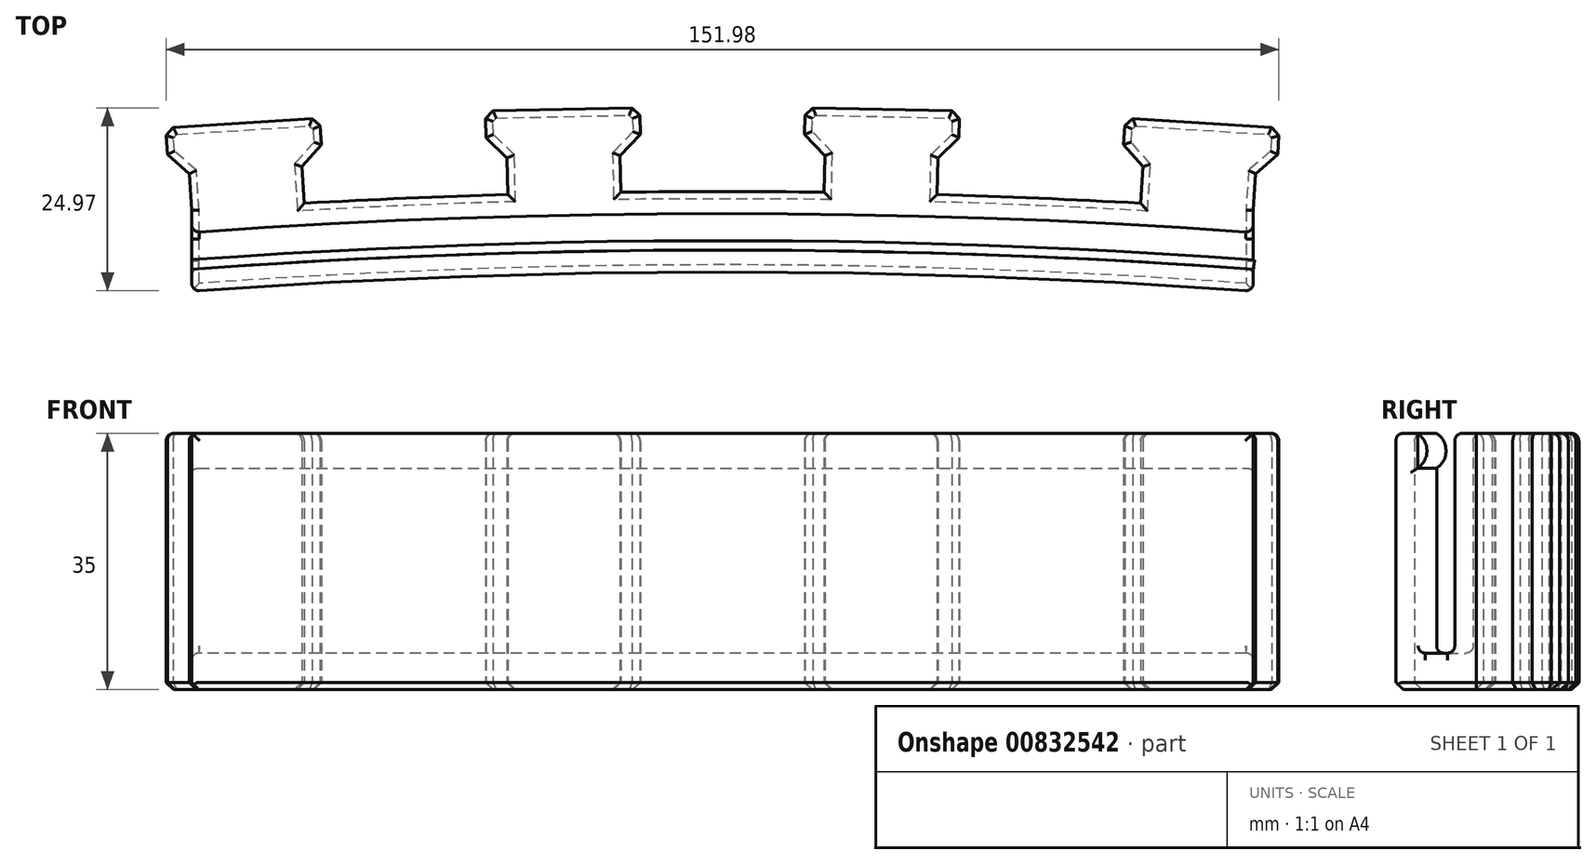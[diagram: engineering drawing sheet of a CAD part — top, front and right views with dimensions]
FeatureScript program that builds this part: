
annotation { "Feature Type Name" : "Feature", "Feature Type Description" : "" }
export const myFeature = defineFeature(function(context is Context, id is Id, definition is map)
    precondition{}
    {
        {
            var Q0;
            Q0=qCreatedBy(makeId("Top.planeOp"),FACE);
            var sketch = newSketch(context, id + "F0", { "sketchPlane" : qUnion([Q0])});
            skArc(sketch, "E0", {"start": v(72.5, 0) * mm, "mid": v(0, 2.6) * mm, "end": v(-72.5, 0) * mm});
            skPoint(sketch, "E1", {"position": v(0, 2.6) * mm});
            skArc(sketch, "E2.0", {"start": v(72.5, 3) * mm, "mid": v(0, 5.6) * mm, "end": v(-72.5, 3) * mm});
            skArc(sketch, "E3.0", {"start": v(72.5, -5.01) * mm, "mid": v(0, -2.4) * mm, "end": v(-72.5, -5.01) * mm});
            skArc(sketch, "E4.0", {"start": v(72.5, -8.02) * mm, "mid": v(0, -5.4) * mm, "end": v(-72.5, -8.02) * mm});
            skLineSegment(sketch, "E5", {"start": v(-72.5, -5.01) * mm, "end": v(-72.5, -8.02) * mm});
            skLineSegment(sketch, "E6", {"start": v(-72.5, 3) * mm, "end": v(-72.5, 0) * mm});
            skLineSegment(sketch, "E7", {"start": v(72.5, 3) * mm, "end": v(72.5, 0) * mm});
            skLineSegment(sketch, "E8", {"start": v(72.5, -5.01) * mm, "end": v(72.5, -8.02) * mm});
            skLineSegment(sketch, "E9", {"start": v(-72.5, 3) * mm, "end": v(-72.5, -8.02) * mm});
            skLineSegment(sketch, "E10", {"start": v(72.5, 3) * mm, "end": v(72.5, -8.02) * mm});
            skPoint(sketch, "E11", {"position": v(-21.6, 5.36) * mm});
            skPoint(sketch, "E12", {"position": v(21.6, 5.36) * mm});
            skSolve(sketch);
        }
        {
            var Q0;
            {var subQ0=sQuery(id+"F0.wireOp",EDGE,"E0");Q0=makeQuery(id+"F0.imprint","IMPRINT",FACE,{"disambiguationData":[TD([[makeQuery(id+"F0.imprint","IMPRINT",EDGE,{"derivedFrom":subQ0}),1.0]])]});}
            var Q1;
            {var subQ0=sQuery(id+"F0.wireOp",EDGE,"E0");Q1=makeQuery(id+"F0.imprint","IMPRINT",FACE,{"disambiguationData":[TD([[makeQuery(id+"F0.imprint","IMPRINT",EDGE,{"derivedFrom":subQ0}),-1.0]])]});}
            var Q2;
            {var subQ0=sQuery(id+"F0.wireOp",EDGE,"E3.0");Q2=makeQuery(id+"F0.imprint","IMPRINT",FACE,{"disambiguationData":[TD([[makeQuery(id+"F0.imprint","IMPRINT",EDGE,{"derivedFrom":subQ0}),1.0]])]});}
            extrude(context, id + "F1", {"entities" : qUnion([Q0, Q1, Q2]), "depth" : 5 * mm, "offsetDistance" : 25 * mm});
        }
        {
            var Q0;
            {var subQ0=sQuery(id+"F0.wireOp",EDGE,"E0");Q0=makeQuery(id+"F0.imprint","IMPRINT",FACE,{"disambiguationData":[TD([[makeQuery(id+"F0.imprint","IMPRINT",EDGE,{"derivedFrom":subQ0}),-1.0]])]});}
            extrude(context, id + "F2", {"entities" : qUnion([Q0]), "operationType" : NewBodyOperationType.ADD, "depth" : 35 * mm, "offsetDistance" : 25 * mm});
        }
        {
            var Q0;
            {var subQ0=sQuery(id+"F0.wireOp",EDGE,"E3.0");Q0=makeQuery(id+"F0.imprint","IMPRINT",FACE,{"disambiguationData":[TD([[makeQuery(id+"F0.imprint","IMPRINT",EDGE,{"derivedFrom":subQ0}),1.0]])]});}
            var Q1;
            Q1=makeQuery(id+"F2.opExtrude","CAP_FACE",FACE,{"disambiguationData":[OSD([sQuery(id+"F0.wireOp",EDGE,"E0"),sQuery(id+"F0.wireOp",EDGE,"E2.0"),sQuery(id+"F0.wireOp",EDGE,"E9"),sQuery(id+"F0.wireOp",EDGE,"E10")])],"isStart":false});
            extrude(context, id + "F3", {"entities" : qUnion([Q0]), "operationType" : NewBodyOperationType.ADD, "endBound" : BoundingType.UP_TO_SURFACE, "depth" : 35 * mm, "endBoundEntityFace" : qUnion([Q1]), "offsetDistance" : 25 * mm});
        }
        {
            var Q0;
            {var subQ0=sQuery(id+"F0.wireOp",EDGE,"E9");Q0=makeQuery(id+"F3.boolean.opBoolean","MERGE",FACE,{"derivedFrom":[makeQuery(id+"F2.boolean.opBoolean","MERGE",FACE,{"derivedFrom":[makeQuery(id+"F1.opExtrude","SWEPT_FACE",FACE,{"disambiguationData":[OSD([subQ0])]}),makeQuery(id+"F2.opExtrude","SWEPT_FACE",FACE,{"disambiguationData":[OSD([subQ0])]})]}),makeQuery(id+"F3.opExtrude","SWEPT_FACE",FACE,{"disambiguationData":[OSD([subQ0])]})]});}
            var sketch = newSketch(context, id + "F4", { "sketchPlane" : qUnion([Q0])});
            skArc(sketch, "E13", {"start": v(5.01, 35) * mm, "mid": v(3.72, 32.62) * mm, "end": v(5.01, 30.24) * mm});
            skSolve(sketch);
        }
        {
            var Q0;
            {var subQ0=sQuery(id+"F4.wireOp",EDGE,"E13");Q0=makeQuery(id+"F4.imprint","IMPRINT",FACE,{"disambiguationData":[TD([[makeQuery(id+"F4.imprint","IMPRINT",EDGE,{"derivedFrom":subQ0}),1.0]])]});}
            var Q1;
            Q1=makeQuery(id+"F3.opExtrude","CAP_EDGE",EDGE,{"disambiguationData":[OSD([sQuery(id+"F0.wireOp",EDGE,"E3.0")])],"isStart":false});
            sweep(context, id + "F5", {"operationType" : NewBodyOperationType.ADD, "profiles" : qUnion([Q0]), "path" : qUnion([Q1])});
        }
        {
            var Q0;
            Q0=qCreatedBy(makeId("Top.planeOp"),FACE);
            var sketch = newSketch(context, id + "F6", { "sketchPlane" : qUnion([Q0])});
            skLineSegment(sketch, "E14", {"start": v(57.11, 3.99) * mm, "end": v(72.5, 3) * mm});
            skLineSegment(sketch, "E15", {"start": v(57.11, 3.99) * mm, "end": v(57.43, 8.98) * mm});
            skLineSegment(sketch, "E16", {"start": v(72.5, 3) * mm, "end": v(72.82, 8) * mm});
            skLineSegment(sketch, "E17", {"start": v(72.82, 8) * mm, "end": v(75.82, 10.64) * mm});
            skLineSegment(sketch, "E18", {"start": v(75.02, 14.36) * mm, "end": v(56.06, 15.57) * mm});
            skLineSegment(sketch, "E19", {"start": v(54.79, 11.98) * mm, "end": v(57.43, 8.98) * mm});
            skLineSegment(sketch, "E20", {"start": v(54.79, 11.98) * mm, "end": v(54.95, 14.6) * mm});
            skLineSegment(sketch, "E21", {"start": v(54.95, 14.6) * mm, "end": v(56.06, 15.57) * mm});
            skLineSegment(sketch, "E22", {"start": v(75.02, 14.36) * mm, "end": v(76, 13.25) * mm});
            skLineSegment(sketch, "E23", {"start": v(76, 13.25) * mm, "end": v(75.82, 10.64) * mm});
            skPoint(sketch, "E24", {"position": v(65.54, 14.96) * mm});
            skPoint(sketch, "E25", {"position": v(64.8, 3.5) * mm});
            skLineSegment(sketch, "E26", {"start": v(66.13, 24.3) * mm, "end": v(62.81, -27.83) * mm, "construction": true});
            skLineSegment(sketch, "E27", {"start": v(53.84, 9.2) * mm, "end": v(75.99, 7.8) * mm, "construction": true});
            skLineSegment(sketch, "E28", {"start": v(54.06, 12.03) * mm, "end": v(76.55, 10.6) * mm, "construction": true});
            skLineSegment(sketch, "E29", {"start": v(57.43, 14.44) * mm, "end": v(80.73, 12.95) * mm, "construction": true});
            skPoint(sketch, "E30", {"position": v(65.3, 11.31) * mm});
            skSolve(sketch);
        }
        {
            var Q0;
            Q0=qCreatedBy(makeId("Top.planeOp"),FACE);
            var sketch = newSketch(context, id + "F7", { "sketchPlane" : qUnion([Q0])});
            skLineSegment(sketch, "E31", {"start": v(-72.5, 3) * mm, "end": v(-57.11, 3.99) * mm});
            skLineSegment(sketch, "E32", {"start": v(-72.5, 3) * mm, "end": v(-72.82, 8) * mm});
            skLineSegment(sketch, "E33", {"start": v(-57.11, 3.99) * mm, "end": v(-57.43, 8.98) * mm});
            skLineSegment(sketch, "E34", {"start": v(-57.43, 8.98) * mm, "end": v(-54.79, 11.98) * mm});
            skLineSegment(sketch, "E35", {"start": v(-56.06, 15.57) * mm, "end": v(-75.02, 14.36) * mm});
            skLineSegment(sketch, "E36", {"start": v(-75.82, 10.64) * mm, "end": v(-72.82, 8) * mm});
            skLineSegment(sketch, "E37", {"start": v(-75.82, 10.64) * mm, "end": v(-76, 13.25) * mm});
            skLineSegment(sketch, "E38", {"start": v(-76, 13.25) * mm, "end": v(-75.02, 14.36) * mm});
            skLineSegment(sketch, "E39", {"start": v(-56.06, 15.57) * mm, "end": v(-54.95, 14.6) * mm});
            skLineSegment(sketch, "E40", {"start": v(-54.95, 14.6) * mm, "end": v(-54.79, 11.98) * mm});
            skPoint(sketch, "E41", {"position": v(-65.54, 14.96) * mm});
            skPoint(sketch, "E42", {"position": v(-64.8, 3.5) * mm});
            skLineSegment(sketch, "E43", {"start": v(-66.36, 27.87) * mm, "end": v(-63.01, -24.64) * mm, "construction": true});
            skLineSegment(sketch, "E44", {"start": v(-77.11, 7.72) * mm, "end": v(-54.85, 9.14) * mm, "construction": true});
            skLineSegment(sketch, "E45", {"start": v(-77.54, 10.53) * mm, "end": v(-55.06, 11.97) * mm, "construction": true});
            skLineSegment(sketch, "E46", {"start": v(-74.75, 13.33) * mm, "end": v(-51.32, 14.83) * mm, "construction": true});
            skPoint(sketch, "E47", {"position": v(-65.3, 11.31) * mm});
            skSolve(sketch);
        }
        {
            var Q0;
            Q0=qCreatedBy(makeId("Top.planeOp"),FACE);
            var sketch = newSketch(context, id + "F8", { "sketchPlane" : qUnion([Q0])});
            skLineSegment(sketch, "E48", {"start": v(-29.3, 5.17) * mm, "end": v(-13.9, 5.5) * mm});
            skLineSegment(sketch, "E49", {"start": v(-29.3, 5.17) * mm, "end": v(-29.41, 10.17) * mm});
            skLineSegment(sketch, "E50", {"start": v(-13.9, 5.5) * mm, "end": v(-14, 10.5) * mm});
            skLineSegment(sketch, "E51", {"start": v(-14, 10.5) * mm, "end": v(-11.23, 13.39) * mm});
            skLineSegment(sketch, "E52", {"start": v(-12.35, 17.02) * mm, "end": v(-31.34, 16.62) * mm});
            skLineSegment(sketch, "E53", {"start": v(-32.3, 12.94) * mm, "end": v(-29.41, 10.17) * mm});
            skLineSegment(sketch, "E54", {"start": v(-32.3, 12.94) * mm, "end": v(-32.36, 15.55) * mm});
            skLineSegment(sketch, "E55", {"start": v(-32.36, 15.55) * mm, "end": v(-31.34, 16.62) * mm});
            skLineSegment(sketch, "E56", {"start": v(-12.35, 17.02) * mm, "end": v(-11.28, 16) * mm});
            skLineSegment(sketch, "E57", {"start": v(-11.28, 16) * mm, "end": v(-11.23, 13.39) * mm});
            skPoint(sketch, "E58", {"position": v(-21.84, 16.82) * mm});
            skPoint(sketch, "E59", {"position": v(-21.6, 5.33) * mm});
            skLineSegment(sketch, "E60", {"start": v(-22.4, 42.7) * mm, "end": v(-21.1, -18.04) * mm, "construction": true});
            skLineSegment(sketch, "E61", {"start": v(-33.71, 10.08) * mm, "end": v(-11.41, 10.55) * mm, "construction": true});
            skLineSegment(sketch, "E62", {"start": v(-34.02, 12.9) * mm, "end": v(-11.5, 13.38) * mm, "construction": true});
            skLineSegment(sketch, "E63", {"start": v(-31.12, 15.58) * mm, "end": v(-7.65, 16.08) * mm, "construction": true});
            skPoint(sketch, "E64", {"position": v(-21.77, 13.16) * mm});
            skSolve(sketch);
        }
        {
            var Q0;
            Q0=qCreatedBy(makeId("Top.planeOp"),FACE);
            var sketch = newSketch(context, id + "F9", { "sketchPlane" : qUnion([Q0])});
            skLineSegment(sketch, "E65", {"start": v(13.9, 5.5) * mm, "end": v(29.3, 5.17) * mm});
            skLineSegment(sketch, "E66", {"start": v(13.9, 5.5) * mm, "end": v(14, 10.5) * mm});
            skLineSegment(sketch, "E67", {"start": v(29.3, 5.17) * mm, "end": v(29.41, 10.17) * mm});
            skLineSegment(sketch, "E68", {"start": v(29.41, 10.17) * mm, "end": v(32.3, 12.94) * mm});
            skLineSegment(sketch, "E69", {"start": v(31.34, 16.62) * mm, "end": v(12.35, 17.02) * mm});
            skLineSegment(sketch, "E70", {"start": v(11.23, 13.39) * mm, "end": v(14, 10.5) * mm});
            skLineSegment(sketch, "E71", {"start": v(11.23, 13.39) * mm, "end": v(11.28, 16) * mm});
            skLineSegment(sketch, "E72", {"start": v(11.28, 16) * mm, "end": v(12.35, 17.02) * mm});
            skLineSegment(sketch, "E73", {"start": v(31.34, 16.62) * mm, "end": v(32.36, 15.55) * mm});
            skLineSegment(sketch, "E74", {"start": v(32.36, 15.55) * mm, "end": v(32.3, 12.94) * mm});
            skPoint(sketch, "E75", {"position": v(21.84, 16.82) * mm});
            skPoint(sketch, "E76", {"position": v(21.6, 5.33) * mm});
            skLineSegment(sketch, "E77", {"start": v(22.43, 44.36) * mm, "end": v(20.9, -27.94) * mm, "construction": true});
            skLineSegment(sketch, "E78", {"start": v(9.7, 10.59) * mm, "end": v(32, 10.11) * mm, "construction": true});
            skLineSegment(sketch, "E79", {"start": v(9.51, 13.42) * mm, "end": v(32.03, 12.94) * mm, "construction": true});
            skLineSegment(sketch, "E80", {"start": v(12.52, 15.98) * mm, "end": v(36, 15.48) * mm, "construction": true});
            skPoint(sketch, "E81", {"position": v(21.77, 13.16) * mm});
            skSolve(sketch);
        }
        {
            var Q0;
            Q0=makeQuery(id+"F7.imprint","IMPRINT",FACE,{"disambiguationData":[TD([[makeQuery(id+"F7.imprint","IMPRINT",EDGE,{"derivedFrom":sQuery(id+"F7.wireOp",EDGE,"E31")}),1.0]])]});
            var Q1;
            Q1=makeQuery(id+"F6.imprint","IMPRINT",FACE,{"disambiguationData":[TD([[makeQuery(id+"F6.imprint","IMPRINT",EDGE,{"derivedFrom":sQuery(id+"F6.wireOp",EDGE,"E14")}),1.0]])]});
            var Q2;
            Q2=makeQuery(id+"F9.imprint","IMPRINT",FACE,{"disambiguationData":[TD([[makeQuery(id+"F9.imprint","IMPRINT",EDGE,{"derivedFrom":sQuery(id+"F9.wireOp",EDGE,"E65")}),1.0]])]});
            var Q3;
            Q3=makeQuery(id+"F8.imprint","IMPRINT",FACE,{"disambiguationData":[TD([[makeQuery(id+"F8.imprint","IMPRINT",EDGE,{"derivedFrom":sQuery(id+"F8.wireOp",EDGE,"E48")}),1.0]])]});
            var Q4;
            Q4=makeQuery(id+"F2.opExtrude","CAP_FACE",FACE,{"disambiguationData":[OSD([sQuery(id+"F0.wireOp",EDGE,"E0"),sQuery(id+"F0.wireOp",EDGE,"E2.0"),sQuery(id+"F0.wireOp",EDGE,"E9"),sQuery(id+"F0.wireOp",EDGE,"E10")])],"isStart":false});
            extrude(context, id + "F10", {"entities" : qUnion([Q0, Q1, Q2, Q3]), "operationType" : NewBodyOperationType.ADD, "endBound" : BoundingType.UP_TO_SURFACE, "depth" : 25 * mm, "endBoundEntityFace" : qUnion([Q4]), "offsetDistance" : 25 * mm});
        }
        {
            var Q0;
            Q0=makeQuery(id+"F10.boolean.opBoolean","MERGE",FACE,{"derivedFrom":[makeQuery(id+"F1.opExtrude","CAP_FACE",FACE,{"disambiguationData":[OSD([sQuery(id+"F0.wireOp",EDGE,"E2.0"),sQuery(id+"F0.wireOp",EDGE,"E4.0"),sQuery(id+"F0.wireOp",EDGE,"E9"),sQuery(id+"F0.wireOp",EDGE,"E10")])],"isStart":true}),makeQuery(id+"F10.opExtrude","CAP_FACE",FACE,{"disambiguationData":[OSD([sQuery(id+"F6.wireOp",EDGE,"E14"),sQuery(id+"F6.wireOp",EDGE,"E15"),sQuery(id+"F6.wireOp",EDGE,"E16"),sQuery(id+"F6.wireOp",EDGE,"E17"),sQuery(id+"F6.wireOp",EDGE,"E18"),sQuery(id+"F6.wireOp",EDGE,"E19"),sQuery(id+"F6.wireOp",EDGE,"E20"),sQuery(id+"F6.wireOp",EDGE,"E21"),sQuery(id+"F6.wireOp",EDGE,"E22"),sQuery(id+"F6.wireOp",EDGE,"E23")])],"isStart":true}),makeQuery(id+"F10.opExtrude","CAP_FACE",FACE,{"disambiguationData":[OSD([sQuery(id+"F7.wireOp",EDGE,"E31"),sQuery(id+"F7.wireOp",EDGE,"E32"),sQuery(id+"F7.wireOp",EDGE,"E33"),sQuery(id+"F7.wireOp",EDGE,"E34"),sQuery(id+"F7.wireOp",EDGE,"E35"),sQuery(id+"F7.wireOp",EDGE,"E36"),sQuery(id+"F7.wireOp",EDGE,"E37"),sQuery(id+"F7.wireOp",EDGE,"E38"),sQuery(id+"F7.wireOp",EDGE,"E39"),sQuery(id+"F7.wireOp",EDGE,"E40")])],"isStart":true}),makeQuery(id+"F10.opExtrude","CAP_FACE",FACE,{"disambiguationData":[OSD([sQuery(id+"F8.wireOp",EDGE,"E48"),sQuery(id+"F8.wireOp",EDGE,"E49"),sQuery(id+"F8.wireOp",EDGE,"E50"),sQuery(id+"F8.wireOp",EDGE,"E51"),sQuery(id+"F8.wireOp",EDGE,"E52"),sQuery(id+"F8.wireOp",EDGE,"E53"),sQuery(id+"F8.wireOp",EDGE,"E54"),sQuery(id+"F8.wireOp",EDGE,"E55"),sQuery(id+"F8.wireOp",EDGE,"E56"),sQuery(id+"F8.wireOp",EDGE,"E57")])],"isStart":true}),makeQuery(id+"F10.opExtrude","CAP_FACE",FACE,{"disambiguationData":[OSD([sQuery(id+"F9.wireOp",EDGE,"E65"),sQuery(id+"F9.wireOp",EDGE,"E66"),sQuery(id+"F9.wireOp",EDGE,"E67"),sQuery(id+"F9.wireOp",EDGE,"E68"),sQuery(id+"F9.wireOp",EDGE,"E69"),sQuery(id+"F9.wireOp",EDGE,"E70"),sQuery(id+"F9.wireOp",EDGE,"E71"),sQuery(id+"F9.wireOp",EDGE,"E72"),sQuery(id+"F9.wireOp",EDGE,"E73"),sQuery(id+"F9.wireOp",EDGE,"E74")])],"isStart":true})]});
            chamfer(context, id + "F11", {"entities" : qUnion([Q0]), "width" : 1 * mm, "tangentPropagation" : true});
        }
        {
            var Q0;
            Q0=makeQuery(id+"F10.boolean.opBoolean","MERGE",FACE,{"derivedFrom":[makeQuery(id+"F2.opExtrude","CAP_FACE",FACE,{"disambiguationData":[OSD([sQuery(id+"F0.wireOp",EDGE,"E0"),sQuery(id+"F0.wireOp",EDGE,"E2.0"),sQuery(id+"F0.wireOp",EDGE,"E9"),sQuery(id+"F0.wireOp",EDGE,"E10")])],"isStart":false}),makeQuery(id+"F10.opExtrude","CAP_FACE",FACE,{"disambiguationData":[OSD([sQuery(id+"F6.wireOp",EDGE,"E14"),sQuery(id+"F6.wireOp",EDGE,"E15"),sQuery(id+"F6.wireOp",EDGE,"E16"),sQuery(id+"F6.wireOp",EDGE,"E17"),sQuery(id+"F6.wireOp",EDGE,"E18"),sQuery(id+"F6.wireOp",EDGE,"E19"),sQuery(id+"F6.wireOp",EDGE,"E20"),sQuery(id+"F6.wireOp",EDGE,"E21"),sQuery(id+"F6.wireOp",EDGE,"E22"),sQuery(id+"F6.wireOp",EDGE,"E23")])],"isStart":false}),makeQuery(id+"F10.opExtrude","CAP_FACE",FACE,{"disambiguationData":[OSD([sQuery(id+"F7.wireOp",EDGE,"E31"),sQuery(id+"F7.wireOp",EDGE,"E32"),sQuery(id+"F7.wireOp",EDGE,"E33"),sQuery(id+"F7.wireOp",EDGE,"E34"),sQuery(id+"F7.wireOp",EDGE,"E35"),sQuery(id+"F7.wireOp",EDGE,"E36"),sQuery(id+"F7.wireOp",EDGE,"E37"),sQuery(id+"F7.wireOp",EDGE,"E38"),sQuery(id+"F7.wireOp",EDGE,"E39"),sQuery(id+"F7.wireOp",EDGE,"E40")])],"isStart":false}),makeQuery(id+"F10.opExtrude","CAP_FACE",FACE,{"disambiguationData":[OSD([sQuery(id+"F8.wireOp",EDGE,"E48"),sQuery(id+"F8.wireOp",EDGE,"E49"),sQuery(id+"F8.wireOp",EDGE,"E50"),sQuery(id+"F8.wireOp",EDGE,"E51"),sQuery(id+"F8.wireOp",EDGE,"E52"),sQuery(id+"F8.wireOp",EDGE,"E53"),sQuery(id+"F8.wireOp",EDGE,"E54"),sQuery(id+"F8.wireOp",EDGE,"E55"),sQuery(id+"F8.wireOp",EDGE,"E56"),sQuery(id+"F8.wireOp",EDGE,"E57")])],"isStart":false}),makeQuery(id+"F10.opExtrude","CAP_FACE",FACE,{"disambiguationData":[OSD([sQuery(id+"F9.wireOp",EDGE,"E65"),sQuery(id+"F9.wireOp",EDGE,"E66"),sQuery(id+"F9.wireOp",EDGE,"E67"),sQuery(id+"F9.wireOp",EDGE,"E68"),sQuery(id+"F9.wireOp",EDGE,"E69"),sQuery(id+"F9.wireOp",EDGE,"E70"),sQuery(id+"F9.wireOp",EDGE,"E71"),sQuery(id+"F9.wireOp",EDGE,"E72"),sQuery(id+"F9.wireOp",EDGE,"E73"),sQuery(id+"F9.wireOp",EDGE,"E74")])],"isStart":false})]});
            var Q1;
            Q1=makeQuery(id+"F3.opExtrude","CAP_EDGE",EDGE,{"disambiguationData":[OSD([sQuery(id+"F0.wireOp",EDGE,"E4.0")])],"isStart":false});
            var Q2;
            {var subQ0=sQuery(id+"F0.wireOp",EDGE,"E9");var subQ1=sQuery(id+"F0.wireOp",EDGE,"E4.0");Q2=makeQuery(id+"F3.boolean.opBoolean","MERGE",EDGE,{"derivedFrom":[makeQuery(id+"F1.opExtrude","SWEPT_EDGE",EDGE,{"disambiguationData":[OSD([subQ1,subQ0])]}),makeQuery(id+"F3.opExtrude","SWEPT_EDGE",EDGE,{"disambiguationData":[OSD([subQ1,subQ0])]})]});}
            var Q3;
            {var subQ0=sQuery(id+"F0.wireOp",EDGE,"E10");var subQ1=sQuery(id+"F0.wireOp",EDGE,"E4.0");Q3=makeQuery(id+"F3.boolean.opBoolean","MERGE",EDGE,{"derivedFrom":[makeQuery(id+"F1.opExtrude","SWEPT_EDGE",EDGE,{"disambiguationData":[OSD([subQ1,subQ0])]}),makeQuery(id+"F3.opExtrude","SWEPT_EDGE",EDGE,{"disambiguationData":[OSD([subQ1,subQ0])]})]});}
            var Q4;
            Q4=makeQuery(id+"F2.opExtrude","SWEPT_EDGE",EDGE,{"disambiguationData":[OSD([sQuery(id+"F0.wireOp",EDGE,"E0"),sQuery(id+"F0.wireOp",EDGE,"E9")])]});
            var Q5;
            Q5=makeQuery(id+"F1.opExtrude","CAP_EDGE",EDGE,{"disambiguationData":[OSD([sQuery(id+"F0.wireOp",EDGE,"E9")])],"isStart":false});
            var Q6;
            Q6=makeQuery(id+"F3.opExtrude","SWEPT_EDGE",EDGE,{"disambiguationData":[OSD([sQuery(id+"F0.wireOp",EDGE,"E3.0"),sQuery(id+"F0.wireOp",EDGE,"E9")])]});
            var Q7;
            Q7=makeQuery(id+"F2.opExtrude","SWEPT_EDGE",EDGE,{"disambiguationData":[OSD([sQuery(id+"F0.wireOp",EDGE,"E0"),sQuery(id+"F0.wireOp",EDGE,"E10")])]});
            var Q8;
            Q8=makeQuery(id+"F1.opExtrude","CAP_EDGE",EDGE,{"disambiguationData":[OSD([sQuery(id+"F0.wireOp",EDGE,"E10")])],"isStart":false});
            var Q9;
            Q9=makeQuery(id+"F5.boolean.opBoolean","SPLIT",EDGE,{"derivedFrom":makeQuery(id+"F3.opExtrude","SWEPT_EDGE",EDGE,{"disambiguationData":[OSD([sQuery(id+"F0.wireOp",EDGE,"E3.0"),sQuery(id+"F0.wireOp",EDGE,"E10")])]})});
            var Q10;
            Q10=makeQuery(id+"F3.boolean.opBoolean","INTERSECT",EDGE,{"derivedFrom":[makeQuery(id+"F1.opExtrude","CAP_FACE",FACE,{"disambiguationData":[OSD([sQuery(id+"F0.wireOp",EDGE,"E2.0"),sQuery(id+"F0.wireOp",EDGE,"E4.0"),sQuery(id+"F0.wireOp",EDGE,"E9"),sQuery(id+"F0.wireOp",EDGE,"E10")])],"isStart":false}),makeQuery(id+"F3.opExtrude","SWEPT_FACE",FACE,{"disambiguationData":[OSD([sQuery(id+"F0.wireOp",EDGE,"E3.0")])]})]});
            var Q11;
            Q11=makeQuery(id+"F2.boolean.opBoolean","INTERSECT",EDGE,{"derivedFrom":[makeQuery(id+"F1.opExtrude","CAP_FACE",FACE,{"disambiguationData":[OSD([sQuery(id+"F0.wireOp",EDGE,"E2.0"),sQuery(id+"F0.wireOp",EDGE,"E4.0"),sQuery(id+"F0.wireOp",EDGE,"E9"),sQuery(id+"F0.wireOp",EDGE,"E10")])],"isStart":false}),makeQuery(id+"F2.opExtrude","SWEPT_FACE",FACE,{"disambiguationData":[OSD([sQuery(id+"F0.wireOp",EDGE,"E0")])]})]});
            fillet(context, id + "F12", {"entities" : qUnion([Q0, Q1, Q2, Q3, Q4, Q5, Q6, Q7, Q8, Q9, Q10, Q11]), "radius" : 1 * mm, "tangentPropagation" : true, "allowEdgeOverflow" : false});
        }
        {
            var Q0;
            Q0=qCreatedBy(makeId("Top.planeOp"),FACE);
            var sketch = newSketch(context, id + "F13", { "sketchPlane" : qUnion([Q0])});
            skPoint(sketch, "E82.0", {"position": v(-65.3, 11.31) * mm});
            skPoint(sketch, "E83.0", {"position": v(-21.77, 13.16) * mm});
            skPoint(sketch, "E84.0", {"position": v(65.3, 11.31) * mm});
            skPoint(sketch, "E84.1", {"position": v(21.77, 13.16) * mm});
            skSolve(sketch);
        }
    });
